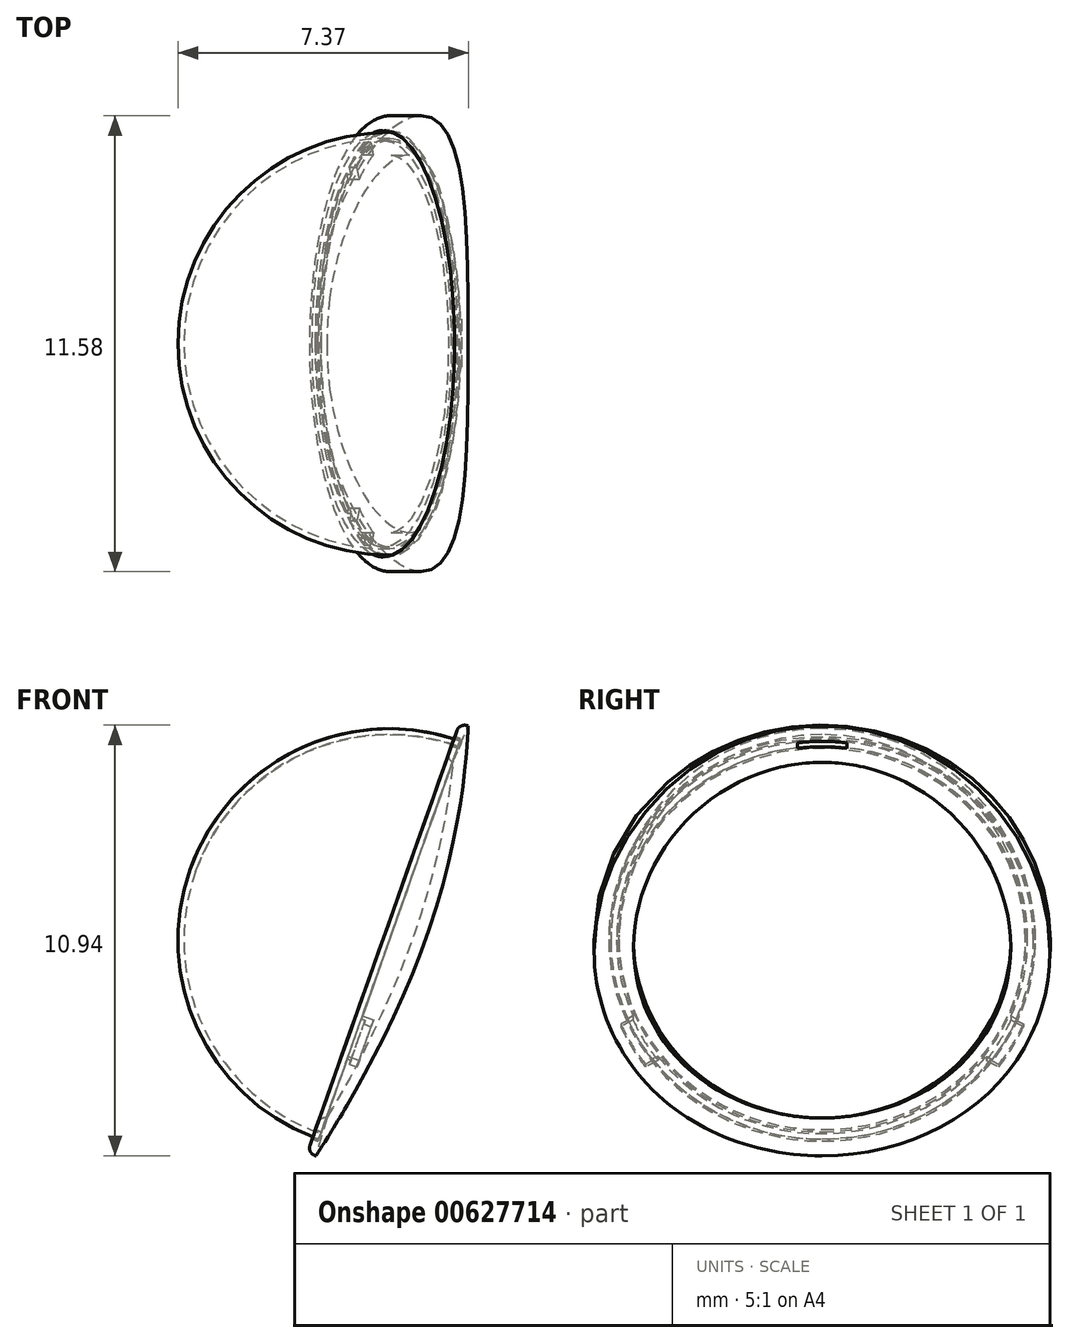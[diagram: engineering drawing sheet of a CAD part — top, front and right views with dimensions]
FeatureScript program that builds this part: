
annotation { "Feature Type Name" : "Feature", "Feature Type Description" : "" }
export const myFeature = defineFeature(function(context is Context, id is Id, definition is map)
    precondition{}
    {
        {
            var Q0;
            Q0=qCreatedBy(makeId("Front.planeOp"),FACE);
            var sketch = newSketch(context, id + "F0", { "sketchPlane" : qUnion([Q0])});
            skLineSegment(sketch, "E0", {"start": v(0, 37.07) * mm, "end": v(0, 0) * mm});
            skLineSegment(sketch, "E1", {"start": v(0, 0) * mm, "end": v(-21.68, 0) * mm});
            skLineSegment(sketch, "E2", {"start": v(0, 37.07) * mm, "end": v(-11.33, 37.07) * mm});
            skArc(sketch, "E3", {"start": v(-11.9, 36.72) * mm, "mid": v(-18.76, 18.89) * mm, "end": v(-21.68, 0) * mm});
            skPoint(sketch, "E4.visualSharp", {"position": v(-11.72, 37.07) * mm});
            skArc(sketch, "E4.filletArc", {"start": v(-11.33, 37.07) * mm, "mid": v(-11.66, 36.98) * mm, "end": v(-11.9, 36.72) * mm});
            skSolve(sketch);
        }
        {
            var Q0;
            Q0=makeQuery(id+"F0.imprint","IMPRINT",FACE,{"disambiguationData":[TD([[makeQuery(id+"F0.imprint","IMPRINT",EDGE,{"derivedFrom":sQuery(id+"F0.wireOp",EDGE,"E0")}),-1.0]])]});
            var Q1;
            {var subQ5=sQuery(id+"F0.wireOp",EDGE,"Yo2jYvwj-cL1Y-x11N-8vAh-q1pDJepjqifZ");Q1=makeQuery(id+"F0.imprint","IMPRINT",FACE,{"disambiguationData":[TD([[makeQuery(id+"F0.imprint","IMPRINT",EDGE,{"derivedFrom":subQ5}),1.0]])]});}
            var Q2;
            Q2=sQuery(id+"F0.wireOp",EDGE,"E0");
            revolve(context, id + "F1", {"entities" : qUnion([Q0, Q1]), "axis" : qUnion([Q2]), "revolveType" : RevolveType.FULL});
        }
        {
            var Q0;
            Q0=qCreatedBy(makeId("Front.planeOp"),FACE);
            var sketch = newSketch(context, id + "F2", { "sketchPlane" : qUnion([Q0])});
            skLineSegment(sketch, "E5", {"start": v(67.56, -4.1) * mm, "end": v(-16.53, 25.69) * mm});
            skLineSegment(sketch, "E6", {"start": v(-14.74, 30.75) * mm, "end": v(-18.33, 20.63) * mm});
            skLineSegment(sketch, "E7", {"start": v(-14.74, 30.75) * mm, "end": v(-14.46, 30.65) * mm});
            skLineSegment(sketch, "E8", {"start": v(-14.46, 30.65) * mm, "end": v(-14.5, 30.5) * mm});
            skLineSegment(sketch, "E9", {"start": v(-14.5, 30.5) * mm, "end": v(-14.8, 30.61) * mm});
            skLineSegment(sketch, "E10", {"start": v(-14.72, 30.8) * mm, "end": v(-18.34, 20.58) * mm});
            skArc(sketch, "E11", {"start": v(-14.72, 30.8) * mm, "mid": v(-21.64, 27.5) * mm, "end": v(-18.34, 20.58) * mm});
            skArc(sketch, "E12", {"start": v(-18.34, 20.58) * mm, "mid": v(-11.42, 23.88) * mm, "end": v(-14.72, 30.8) * mm, "construction": true});
            skArc(sketch, "E13", {"start": v(-18.33, 20.63) * mm, "mid": v(-11.47, 23.9) * mm, "end": v(-14.74, 30.75) * mm, "construction": true});
            skArc(sketch, "E14", {"start": v(-14.74, 30.75) * mm, "mid": v(-21.6, 27.48) * mm, "end": v(-18.33, 20.63) * mm});
            skArc(sketch, "E15", {"start": v(-18.28, 20.77) * mm, "mid": v(-11.61, 23.95) * mm, "end": v(-14.8, 30.61) * mm, "construction": true});
            skArc(sketch, "E16", {"start": v(-14.8, 30.61) * mm, "mid": v(-21.45, 27.43) * mm, "end": v(-18.28, 20.77) * mm});
            skArc(sketch, "E17", {"start": v(-14.8, 30.56) * mm, "mid": v(-21.4, 27.42) * mm, "end": v(-18.26, 20.82) * mm});
            skArc(sketch, "E18", {"start": v(-18.26, 20.82) * mm, "mid": v(-11.66, 23.96) * mm, "end": v(-14.8, 30.56) * mm, "construction": true});
            skLineSegment(sketch, "E19", {"start": v(-14.46, 30.65) * mm, "end": v(-14.39, 30.85) * mm});
            skLineSegment(sketch, "E20", {"start": v(-14.39, 30.85) * mm, "end": v(-14.58, 30.92) * mm});
            skLineSegment(sketch, "E21", {"start": v(-14.58, 30.92) * mm, "end": v(-14.65, 30.72) * mm});
            skLineSegment(sketch, "E22", {"start": v(-16.53, 25.69) * mm, "end": v(-21.64, 27.5) * mm});
            skLineSegment(sketch, "E23", {"start": v(-18.5, 20.64) * mm, "end": v(-18.62, 20.28) * mm});
            skLineSegment(sketch, "E24", {"start": v(-18.62, 20.28) * mm, "end": v(-18.43, 20.22) * mm});
            skLineSegment(sketch, "E25", {"start": v(-18.43, 20.22) * mm, "end": v(-18.1, 21.16) * mm});
            skLineSegment(sketch, "E26", {"start": v(-18.1, 21.16) * mm, "end": v(-18.28, 21.23) * mm});
            skLineSegment(sketch, "E27", {"start": v(-18.28, 21.23) * mm, "end": v(-18.4, 20.87) * mm});
            skLineSegment(sketch, "E28", {"start": v(-18.1, 21.16) * mm, "end": v(-12.06, 19.02) * mm});
            skLineSegment(sketch, "E29", {"start": v(-12.06, 19.02) * mm, "end": v(-12.4, 18.08) * mm});
            skLineSegment(sketch, "E30", {"start": v(-18.43, 20.22) * mm, "end": v(-12.4, 18.08) * mm});
            skPoint(sketch, "E31", {"position": v(-18.26, 20.69) * mm});
            skSolve(sketch);
        }
        {
            var Q0;
            Q0=qCreatedBy(makeId("Front.planeOp"),FACE);
            var sketch = newSketch(context, id + "F3", { "sketchPlane" : qUnion([Q0])});
            skLineSegment(sketch, "E32.bottom", {"start": v(-69.64, 70.3) * mm, "end": v(91.87, 70.3) * mm});
            skLineSegment(sketch, "E32.top", {"start": v(-69.64, -66.65) * mm, "end": v(91.87, -66.65) * mm});
            skLineSegment(sketch, "E32.left", {"start": v(-69.64, 70.3) * mm, "end": v(-69.64, -66.65) * mm});
            skLineSegment(sketch, "E32.right", {"start": v(91.87, 70.3) * mm, "end": v(91.87, -66.65) * mm});
            skSolve(sketch);
        }
        {
            var Q0;
            {var subQ0=sQuery(id+"F2.wireOp",EDGE,"E8");Q0=makeQuery(id+"F2.imprint","IMPRINT",FACE,{"disambiguationData":[TD([[makeQuery(id+"F2.imprint","IMPRINT",EDGE,{"derivedFrom":subQ0}),-1.0]])]});}
            var Q1;
            {var subQ0=sQuery(id+"F2.wireOp",EDGE,"E19");Q1=makeQuery(id+"F2.imprint","IMPRINT",FACE,{"disambiguationData":[TD([[makeQuery(id+"F2.imprint","IMPRINT",EDGE,{"derivedFrom":subQ0}),1.0]])]});}
            var Q2;
            Q2=sQuery(id+"F2.wireOp",EDGE,"E5");
            revolve(context, id + "F4", {"entities" : qUnion([Q0, Q1]), "axis" : qUnion([Q2]), "revolveType" : RevolveType.TWO_DIRECTIONS, "angle" : 30 * degree, "angleBack" : 330 * degree});
        }
        {
            var Q0;
            Q0=makeQuery(id+"F3.imprint","IMPRINT",FACE,{"disambiguationData":[TD([[makeQuery(id+"F3.imprint","IMPRINT",EDGE,{"derivedFrom":sQuery(id+"F3.wireOp",EDGE,"E32.bottom")}),-1.0]])]});
            extrude(context, id + "F5", {"entities" : qUnion([Q0]), "operationType" : NewBodyOperationType.INTERSECT, "endBound" : BoundingType.SYMMETRIC, "depth" : 1.25 * mm, "offsetDistance" : 25 * mm, "hasSecondDirection" : true, "secondDirectionOppositeDirection" : true, "secondDirectionDepth" : 25 * mm});
        }
        {
            var Q0;
            Q0=makeQuery(id+"F4.opRevolve","SWEPT_BODY",BODY,{"disambiguationData":[OSD([sQuery(id+"F2.wireOp",EDGE,"E6"),sQuery(id+"F2.wireOp",EDGE,"E7"),sQuery(id+"F2.wireOp",EDGE,"E8"),sQuery(id+"F2.wireOp",EDGE,"E9"),sQuery(id+"F2.wireOp",EDGE,"E19"),sQuery(id+"F2.wireOp",EDGE,"E20"),sQuery(id+"F2.wireOp",EDGE,"E21")])]});
            var Q1;
            Q1=sQuery(id+"F2.wireOp",EDGE,"E5");
            circularPattern(context, id + "F6", {"entities" : qUnion([Q0]), "axis" : qUnion([Q1]), "angle" : 360 * degree, "instanceCount" : 3, "equalSpace" : true});
        }
        {
            var Q0;
            {var subQ0=sQuery(id+"F2.wireOp",EDGE,"E14");var subQ5=sQuery(id+"F2.wireOp",EDGE,"E22");var subQ6=makeQuery(id+"F2.imprint","INTERSECT",VERTEX,{"derivedFrom":[subQ0,subQ5]});Q0=makeQuery(id+"F2.imprint","IMPRINT",FACE,{"disambiguationData":[TD([[makeQuery(id+"F2.imprint","IMPRINT",EDGE,{"disambiguationData":[TD([[subQ6,1.0]])],"derivedFrom":subQ5}),-1.0]])]});}
            var Q1;
            Q1=sQuery(id+"F2.wireOp",EDGE,"E22");
            revolve(context, id + "F7", {"operationType" : NewBodyOperationType.ADD, "entities" : qUnion([Q0]), "axis" : qUnion([Q1]), "revolveType" : RevolveType.FULL});
        }
        {
            var Q0;
            {var subQ9=sQuery(id+"F2.wireOp",EDGE,"E23");Q0=makeQuery(id+"F2.imprint","IMPRINT",FACE,{"disambiguationData":[TD([[makeQuery(id+"F2.imprint","IMPRINT",EDGE,{"derivedFrom":subQ9}),1.0]])]});}
            var Q1;
            Q1=makeQuery(id+"F2.imprint","IMPRINT",FACE,{"disambiguationData":[TD([[makeQuery(id+"F2.imprint","IMPRINT",EDGE,{"derivedFrom":sQuery(id+"F2.wireOp",EDGE,"E25")}),-1.0]])]});
            var Q2;
            {var subQ5=sQuery(id+"F2.wireOp",EDGE,"E27");Q2=makeQuery(id+"F2.imprint","IMPRINT",FACE,{"disambiguationData":[TD([[makeQuery(id+"F2.imprint","IMPRINT",EDGE,{"derivedFrom":subQ5}),1.0]])]});}
            var Q3;
            Q3=sQuery(id+"F2.wireOp",EDGE,"E5");
            revolve(context, id + "F8", {"entities" : qUnion([Q0, Q1, Q2]), "axis" : qUnion([Q3]), "revolveType" : RevolveType.FULL});
        }
        {
            var Q0;
            Q0=makeQuery(id+"F0.imprint","IMPRINT",FACE,{"disambiguationData":[TD([[makeQuery(id+"F0.imprint","IMPRINT",EDGE,{"derivedFrom":sQuery(id+"F0.wireOp",EDGE,"E0")}),-1.0]])]});
            var Q1;
            Q1=sQuery(id+"F0.wireOp",EDGE,"E0");
            revolve(context, id + "F9", {"operationType" : NewBodyOperationType.REMOVE, "entities" : qUnion([Q0]), "axis" : qUnion([Q1]), "revolveType" : RevolveType.FULL, "oppositeDirection" : true});
        }
        {
            var Q0;
            Q0=makeQuery(id+"F8.opRevolve","SWEPT_EDGE",EDGE,{"disambiguationData":[OSD([sQuery(id+"F2.wireOp",EDGE,"E23"),sQuery(id+"F2.wireOp",EDGE,"E24")])]});
            var Q1;
            Q1=makeQuery(id+"F8.opRevolve","SWEPT_EDGE",EDGE,{"disambiguationData":[OSD([sQuery(id+"F2.wireOp",EDGE,"E26"),sQuery(id+"F2.wireOp",EDGE,"E27")])]});
            fillet(context, id + "F10", {"entities" : qUnion([Q0, Q1]), "radius" : .2 * mm, "tangentPropagation" : true, "allowEdgeOverflow" : false});
        }
    });
